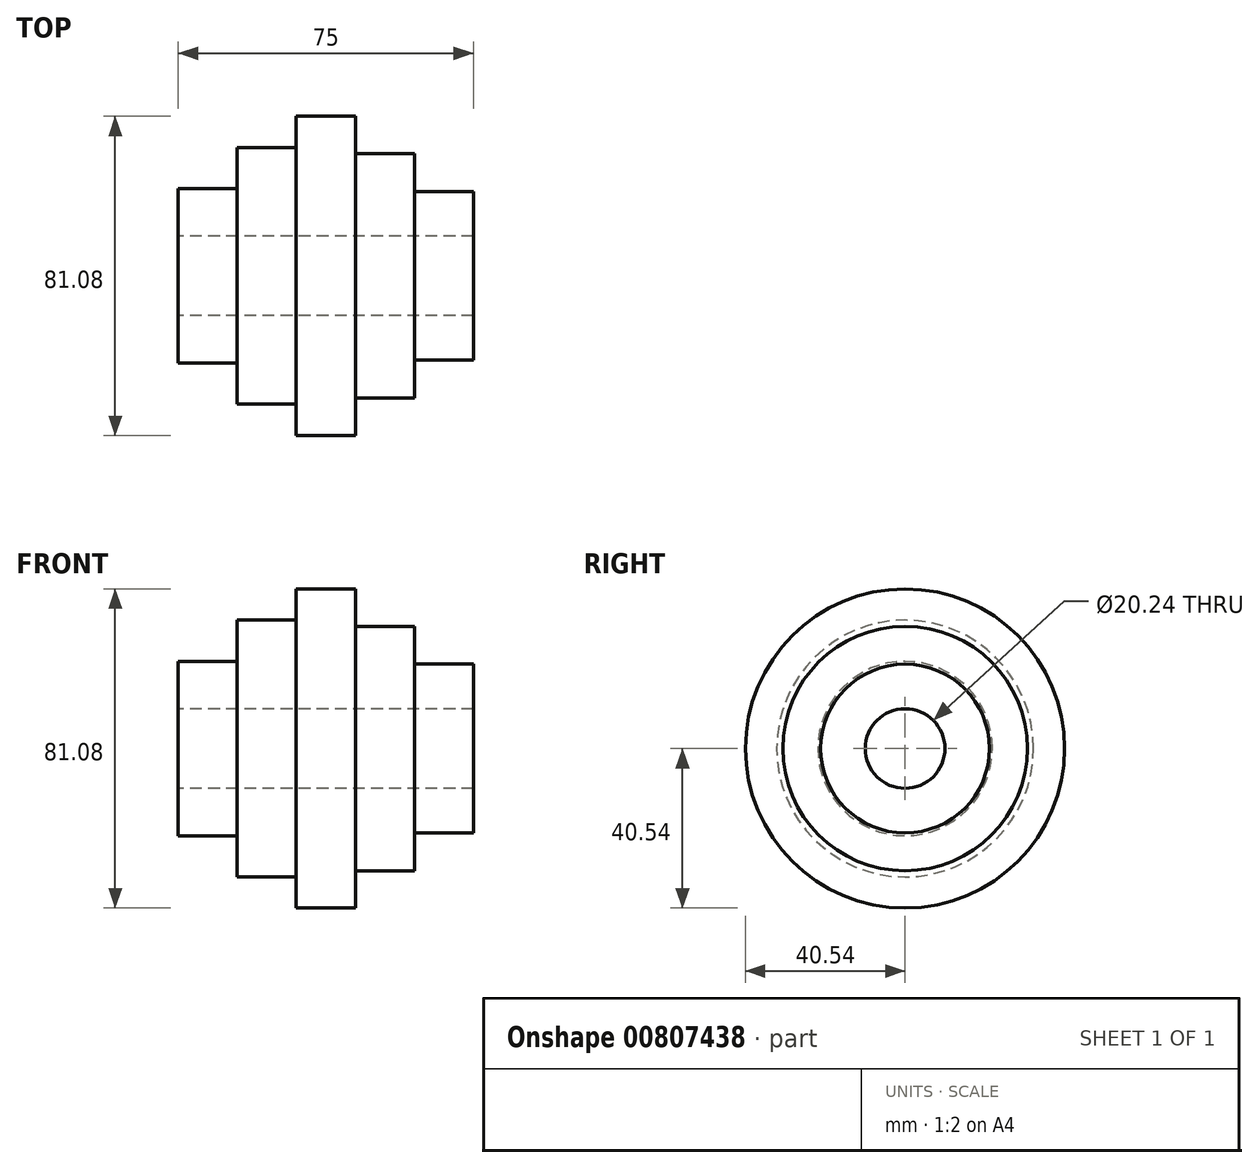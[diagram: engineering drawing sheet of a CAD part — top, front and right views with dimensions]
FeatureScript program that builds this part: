
annotation { "Feature Type Name" : "Feature", "Feature Type Description" : "" }
export const myFeature = defineFeature(function(context is Context, id is Id, definition is map)
    precondition{}
    {
        {
            var Q0;
            Q0=qCreatedBy(makeId("Front.planeOp"),FACE);
            var sketch = newSketch(context, id + "F0", { "sketchPlane" : qUnion([Q0])});
            skLineSegment(sketch, "E0", {"start": v(-56.4, 0) * mm, "end": v(56.96, 0) * mm, "construction": true});
            skLineSegment(sketch, "E1", {"start": v(37.5, 10.12) * mm, "end": v(37.5, 21.44) * mm});
            skLineSegment(sketch, "E2", {"start": v(37.5, 21.44) * mm, "end": v(22.5, 21.44) * mm});
            skLineSegment(sketch, "E3", {"start": v(22.5, 21.44) * mm, "end": v(22.5, 31.06) * mm});
            skLineSegment(sketch, "E4", {"start": v(22.5, 31.06) * mm, "end": v(7.5, 31.06) * mm});
            skLineSegment(sketch, "E5", {"start": v(7.5, 31.06) * mm, "end": v(7.5, 40.54) * mm});
            skLineSegment(sketch, "E6", {"start": v(7.5, 40.54) * mm, "end": v(-7.5, 40.54) * mm});
            skLineSegment(sketch, "E7", {"start": v(-7.5, 40.54) * mm, "end": v(-7.5, 32.62) * mm});
            skLineSegment(sketch, "E8", {"start": v(-7.5, 32.62) * mm, "end": v(-22.5, 32.62) * mm});
            skLineSegment(sketch, "E9", {"start": v(-22.5, 32.62) * mm, "end": v(-22.5, 22.15) * mm});
            skLineSegment(sketch, "E10", {"start": v(-22.5, 22.15) * mm, "end": v(-37.5, 22.15) * mm});
            skLineSegment(sketch, "E11", {"start": v(-37.5, 22.15) * mm, "end": v(-37.5, 10.12) * mm});
            skLineSegment(sketch, "E12", {"start": v(-37.5, 10.12) * mm, "end": v(37.5, 10.12) * mm});
            skSolve(sketch);
        }
        {
            var Q0;
            Q0=makeQuery(id+"F0.imprint","IMPRINT",FACE,{"disambiguationData":[TD([[makeQuery(id+"F0.imprint","IMPRINT",EDGE,{"derivedFrom":sQuery(id+"F0.wireOp",EDGE,"E1")}),1.0]])]});
            var Q1;
            Q1=sQuery(id+"F0.wireOp",EDGE,"E0");
            revolve(context, id + "F1", {"surfaceOperationType" : NewSurfaceOperationType.NEW, "entities" : qUnion([Q0]), "axis" : qUnion([Q1]), "revolveType" : RevolveType.FULL});
        }
    });
